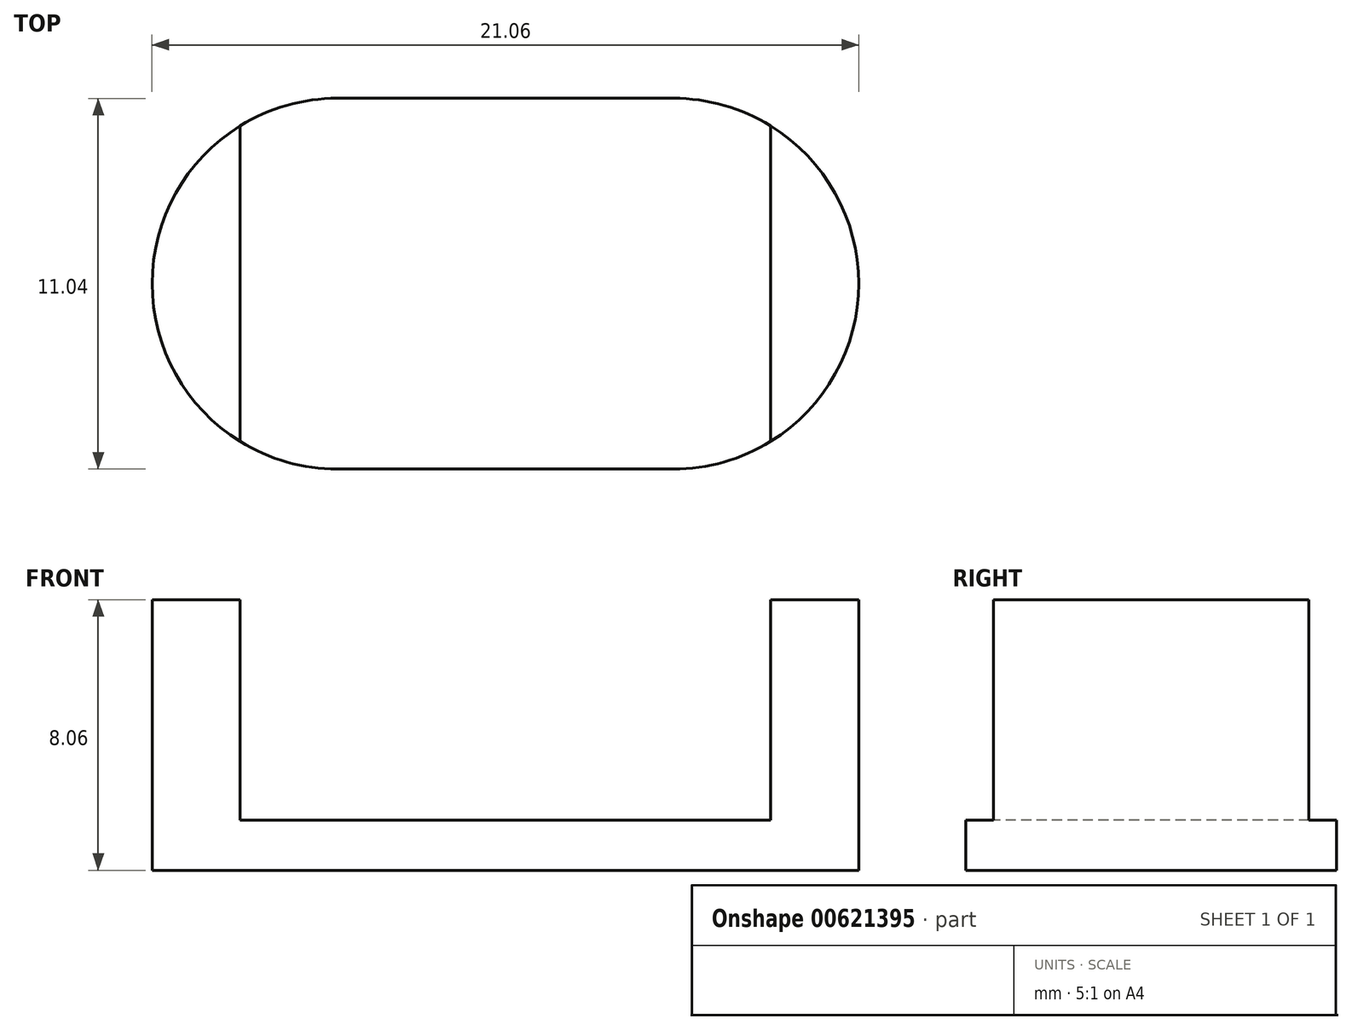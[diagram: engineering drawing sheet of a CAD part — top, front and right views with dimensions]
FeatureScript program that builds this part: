
annotation { "Feature Type Name" : "Feature", "Feature Type Description" : "" }
export const myFeature = defineFeature(function(context is Context, id is Id, definition is map)
    precondition{}
    {
        {
            var Q0;
            Q0=qCreatedBy(makeId("Top.planeOp"),FACE);
            var sketch = newSketch(context, id + "F0", { "sketchPlane" : qUnion([Q0])});
            skLineSegment(sketch, "E0.bottom", {"start": v(5, 5.52) * mm, "end": v(-5, 5.52) * mm});
            skLineSegment(sketch, "E0.top", {"start": v(5, -5.52) * mm, "end": v(-5, -5.52) * mm});
            skPoint(sketch, "E0.middle", {"position": v(0, 0) * mm});
            skArc(sketch, "E1", {"start": v(5, -5.52) * mm, "mid": v(10.53, 0) * mm, "end": v(5, 5.52) * mm});
            skPoint(sketch, "E1.first.point", {"position": v(5, 5.52) * mm});
            skPoint(sketch, "E1.second.point", {"position": v(10.53, 0) * mm});
            skPoint(sketch, "E1.third.point", {"position": v(5, -5.52) * mm});
            skArc(sketch, "E2", {"start": v(-5, 5.52) * mm, "mid": v(-10.53, 0) * mm, "end": v(-5, -5.52) * mm});
            skPoint(sketch, "E2.first.point", {"position": v(-5, 5.52) * mm});
            skPoint(sketch, "E2.second.point", {"position": v(-10.53, 0) * mm});
            skPoint(sketch, "E2.third.point", {"position": v(-5, -5.52) * mm});
            skPoint(sketch, "E3.orphan", {"position": v(-10.53, 5.52) * mm});
            skPoint(sketch, "E4.orphan", {"position": v(-10.53, -5.52) * mm});
            skPoint(sketch, "E5.orphan", {"position": v(10.53, 5.52) * mm});
            skPoint(sketch, "E0.left.end.orphan", {"position": v(10.53, -5.52) * mm});
            skPoint(sketch, "E6", {"position": v(0, 5.52) * mm});
            skPoint(sketch, "E7", {"position": v(0, -5.52) * mm});
            skSolve(sketch);
        }
        {
            var Q0;
            Q0 = qSketchRegion(id + "F0", true);
            extrude(context, id + "F1", {"entities" : qUnion([Q0]), "depth" : 8.06 * mm, "offsetDistance" : 25.4 * mm});
        }
        {
            var Q0;
            Q0=makeQuery(id+"F1.opExtrude","CAP_FACE",FACE,{"disambiguationData":[OSD([sQuery(id+"F0.wireOp",EDGE,"E0.bottom"),sQuery(id+"F0.wireOp",EDGE,"E0.top"),sQuery(id+"F0.wireOp",EDGE,"E1"),sQuery(id+"F0.wireOp",EDGE,"E2")])],"isStart":false});
            var sketch = newSketch(context, id + "F2", { "sketchPlane" : qUnion([Q0])});
            skLineSegment(sketch, "E8.bottom", {"start": v(7.9, 12.31) * mm, "end": v(-7.9, 12.31) * mm});
            skLineSegment(sketch, "E8.top", {"start": v(7.9, -12.31) * mm, "end": v(-7.9, -12.31) * mm});
            skLineSegment(sketch, "E8.left", {"start": v(7.9, 12.31) * mm, "end": v(7.9, -12.31) * mm});
            skLineSegment(sketch, "E8.right", {"start": v(-7.9, 12.31) * mm, "end": v(-7.9, -12.31) * mm});
            skPoint(sketch, "E8.middle", {"position": v(0, 0) * mm});
            skSolve(sketch);
        }
        {
            var Q0;
            {var subQ5=makeQuery(id+"F1.opExtrude","CAP_EDGE",EDGE,{"disambiguationData":[OSD([sQuery(id+"F0.wireOp",EDGE,"E0.bottom")])],"isStart":false});Q0=makeQuery(id+"F2.imprint","IMPRINT",FACE,{"disambiguationData":[TD([[makeQuery(id+"F2.imprint","IMPRINT",EDGE,{"derivedFrom":subQ5}),1.0]])]});}
            extrude(context, id + "F3", {"entities" : qUnion([Q0]), "operationType" : NewBodyOperationType.REMOVE, "oppositeDirection" : true, "depth" : 6.57 * mm, "offsetDistance" : 25.4 * mm});
        }
    });
